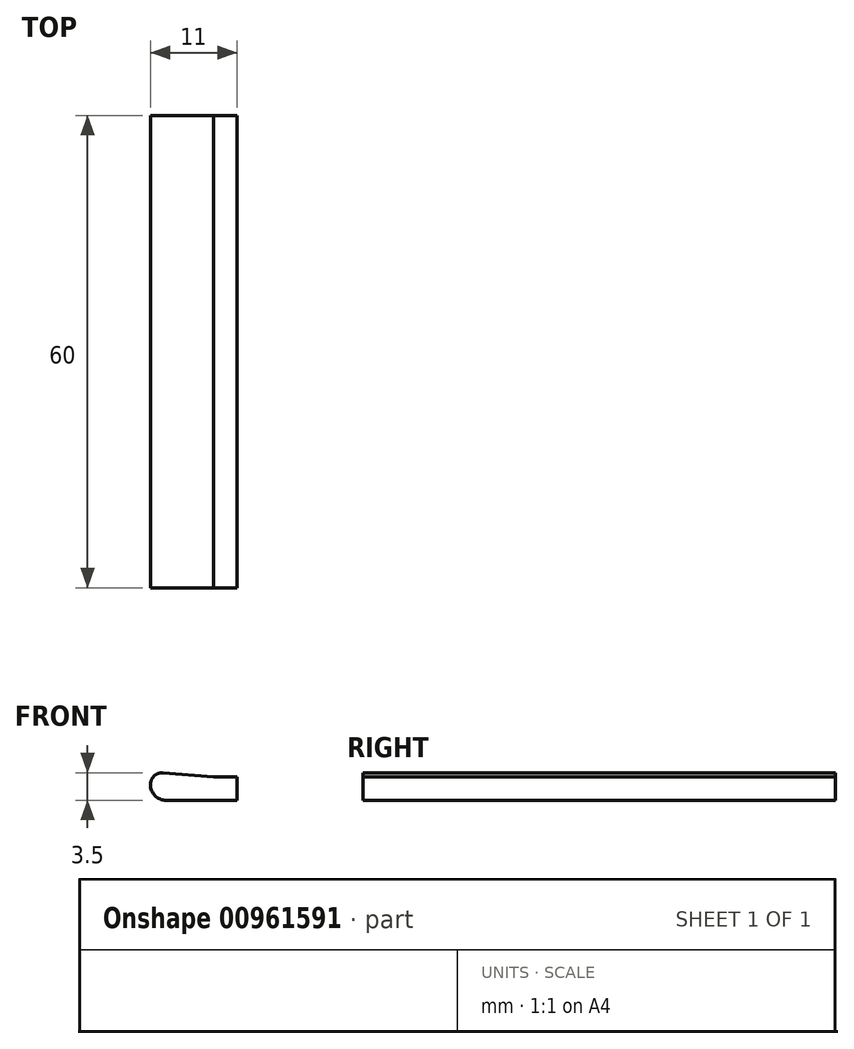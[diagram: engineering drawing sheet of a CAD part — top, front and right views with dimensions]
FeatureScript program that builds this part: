
annotation { "Feature Type Name" : "Feature", "Feature Type Description" : "" }
export const myFeature = defineFeature(function(context is Context, id is Id, definition is map)
    precondition{}
    {
        {
            var Q0;
            Q0=qCreatedBy(makeId("Front.planeOp"),FACE);
            var sketch = newSketch(context, id + "F0", { "sketchPlane" : qUnion([Q0])});
            skLineSegment(sketch, "E0", {"start": v(0, 0) * mm, "end": v(0, 3) * mm});
            skLineSegment(sketch, "E1", {"start": v(0, 0) * mm, "end": v(-6, 0) * mm});
            skLineSegment(sketch, "E2", {"start": v(0, 3) * mm, "end": v(-6.38, 3.5) * mm});
            skArc(sketch, "E3", {"start": v(-6.38, 3.5) * mm, "mid": v(-7.52, 3.1) * mm, "end": v(-8, 2) * mm});
            skArc(sketch, "E4", {"start": v(-8, 2) * mm, "mid": v(-7.41, 0.59) * mm, "end": v(-6, 0) * mm});
            skSolve(sketch);
        }
        {
            var Q0;
            Q0=makeQuery(id+"F0.imprint","IMPRINT",FACE,{"disambiguationData":[TD([[makeQuery(id+"F0.imprint","IMPRINT",EDGE,{"derivedFrom":sQuery(id+"F0.wireOp",EDGE,"E0")}),1.0]])]});
            extrude(context, id + "F1", {"entities" : qUnion([Q0]), "depth" : 60 * mm, "offsetDistance" : 25 * mm});
        }
        {
            var Q0;
            Q0=makeQuery(id+"F1.opExtrude","CAP_FACE",FACE,{"disambiguationData":[OSD([sQuery(id+"F0.wireOp",EDGE,"E0"),sQuery(id+"F0.wireOp",EDGE,"E1"),sQuery(id+"F0.wireOp",EDGE,"E2"),sQuery(id+"F0.wireOp",EDGE,"E3"),sQuery(id+"F0.wireOp",EDGE,"E4")])],"isStart":false});
            var sketch = newSketch(context, id + "F2", { "sketchPlane" : qUnion([Q0])});
            skLineSegment(sketch, "E5.bottom", {"start": v(0, 3) * mm, "end": v(3, 3) * mm});
            skLineSegment(sketch, "E5.top", {"start": v(0, 0) * mm, "end": v(3, 0) * mm});
            skLineSegment(sketch, "E5.left", {"start": v(0, 3) * mm, "end": v(0, 0) * mm});
            skLineSegment(sketch, "E5.right", {"start": v(3, 3) * mm, "end": v(3, 0) * mm});
            skSolve(sketch);
        }
        {
            var Q0;
            Q0=qSketchRegion(id+"F2",true);
            extrude(context, id + "F3", {"entities" : qUnion([Q0]), "operationType" : NewBodyOperationType.ADD, "depth" : -60 * mm, "offsetDistance" : 25 * mm});
        }
        {
            var Q0;
            Q0=makeQuery(id+"F3.boolean.opBoolean","MERGE",FACE,{"derivedFrom":[makeQuery(id+"F1.opExtrude","CAP_FACE",FACE,{"disambiguationData":[OSD([sQuery(id+"F0.wireOp",EDGE,"E0"),sQuery(id+"F0.wireOp",EDGE,"E1"),sQuery(id+"F0.wireOp",EDGE,"E2"),sQuery(id+"F0.wireOp",EDGE,"E3"),sQuery(id+"F0.wireOp",EDGE,"E4")])],"isStart":false}),makeQuery(id+"F3.opExtrude","CAP_FACE",FACE,{"disambiguationData":[OSD([sQuery(id+"F2.wireOp",EDGE,"E5.bottom"),sQuery(id+"F2.wireOp",EDGE,"E5.top"),sQuery(id+"F2.wireOp",EDGE,"E5.left"),sQuery(id+"F2.wireOp",EDGE,"E5.right")])],"isStart":true})]});
            extrude(context, id + "F4", {"entities" : qUnion([Q0]), "operationType" : NewBodyOperationType.REMOVE, "oppositeDirection" : true, "depth" : 42 * mm, "offsetDistance" : 25 * mm});
        }
        {
            var Q0;
            Q0=makeQuery(id+"F4.boolean.opBoolean","COPY",FACE,{"derivedFrom":makeQuery(id+"F4.opExtrude","CAP_FACE",FACE,{"disambiguationData":[OSD([sQuery(id+"F0.wireOp",EDGE,"E0"),sQuery(id+"F0.wireOp",EDGE,"E1"),sQuery(id+"F0.wireOp",EDGE,"E2"),sQuery(id+"F0.wireOp",EDGE,"E3"),sQuery(id+"F0.wireOp",EDGE,"E4"),sQuery(id+"F2.wireOp",EDGE,"E5.bottom"),sQuery(id+"F2.wireOp",EDGE,"E5.top"),sQuery(id+"F2.wireOp",EDGE,"E5.left"),sQuery(id+"F2.wireOp",EDGE,"E5.right")])],"isStart":false})});
            extrude(context, id + "F5", {"entities" : qUnion([Q0]), "operationType" : NewBodyOperationType.ADD, "depth" : 35 * mm, "offsetDistance" : 25 * mm});
        }
        {
            var Q0;
            Q0=makeQuery(id+"F5.opExtrude","CAP_FACE",FACE,{"disambiguationData":[OSD([sQuery(id+"F0.wireOp",EDGE,"E0"),sQuery(id+"F0.wireOp",EDGE,"E1"),sQuery(id+"F0.wireOp",EDGE,"E2"),sQuery(id+"F0.wireOp",EDGE,"E3"),sQuery(id+"F0.wireOp",EDGE,"E4"),sQuery(id+"F2.wireOp",EDGE,"E5.bottom"),sQuery(id+"F2.wireOp",EDGE,"E5.top"),sQuery(id+"F2.wireOp",EDGE,"E5.left"),sQuery(id+"F2.wireOp",EDGE,"E5.right")])],"isStart":false});
            extrude(context, id + "F6", {"entities" : qUnion([Q0]), "operationType" : NewBodyOperationType.ADD, "depth" : 7 * mm, "offsetDistance" : 25 * mm});
        }
    });
